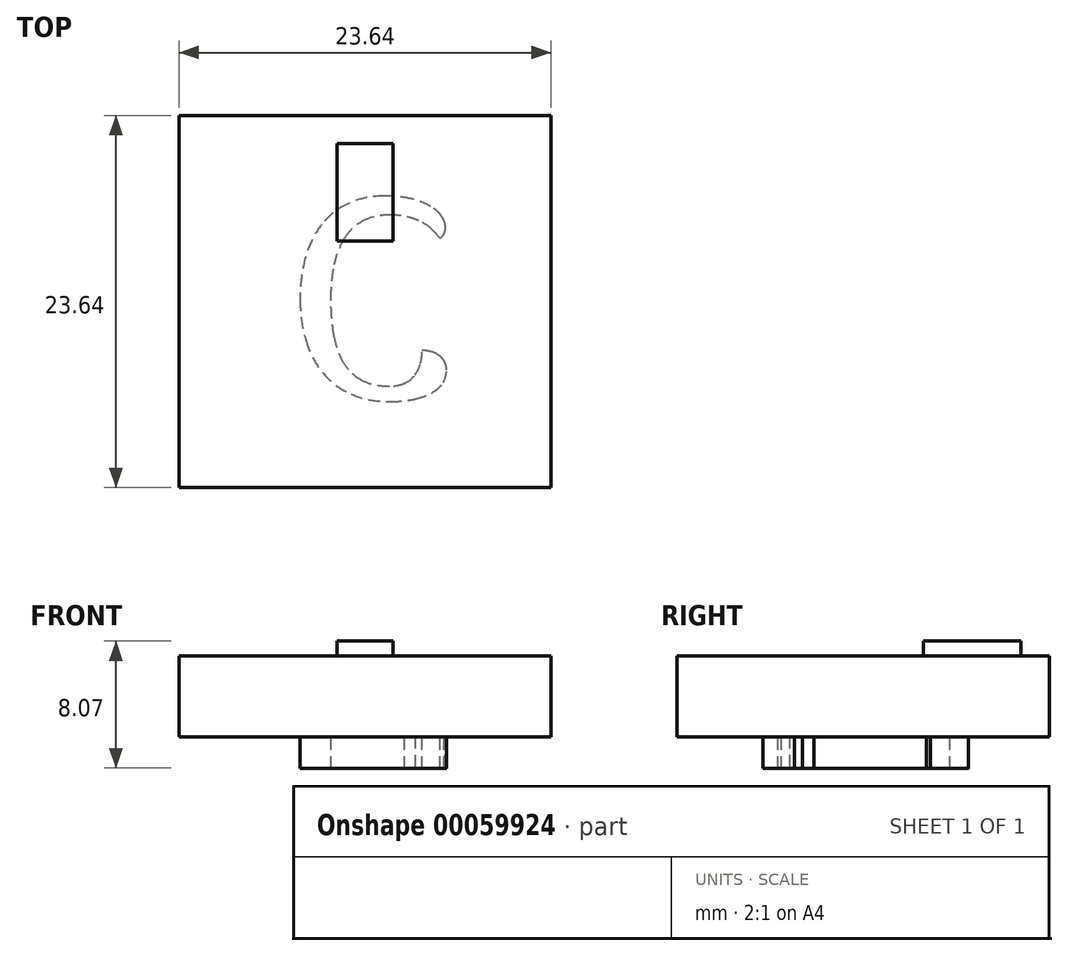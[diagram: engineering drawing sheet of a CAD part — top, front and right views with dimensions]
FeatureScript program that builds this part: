
annotation { "Feature Type Name" : "Feature", "Feature Type Description" : "" }
export const myFeature = defineFeature(function(context is Context, id is Id, definition is map)
    precondition{}
    {
        {
            var Q0;
            Q0=qCreatedBy(makeId("Top.planeOp"),FACE);
            var sketch = newSketch(context, id + "F0", { "sketchPlane" : qUnion([Q0])});
            skCircle(sketch, "E0.cCircle", {"center": v(0, 0) * mm, "radius": 11.82 * mm, "construction": true});
            skLineSegment(sketch, "E0.0", {"start": v(-11.82, 11.82) * mm, "end": v(11.82, 11.82) * mm});
            skLineSegment(sketch, "E0.1", {"start": v(11.82, 11.82) * mm, "end": v(11.82, -11.82) * mm});
            skLineSegment(sketch, "E0.2", {"start": v(11.82, -11.82) * mm, "end": v(-11.82, -11.82) * mm});
            skLineSegment(sketch, "E0.3", {"start": v(-11.82, -11.82) * mm, "end": v(-11.82, 11.82) * mm});
            skPoint(sketch, "E0.0.midPoint", {"position": v(0, 11.82) * mm});
            skSolve(sketch);
        }
        {
            var Q0;
            Q0 = qSketchRegion(id + "F0", true);
            var Q1;
            Q1 = qConstructionFilter(qBodyType(qCreatedBy(id + "F0" ,EDGE), BodyType.WIRE), ConstructionObject.NO);
            extrude(context, id + "F1", {"entities" : qUnion([Q0]), "surfaceEntities" : qUnion([Q1]), "endBound" : BoundingType.SYMMETRIC, "depth" : 5.14 * mm});
        }
        {
            var Q0;
            Q0=qCreatedBy(makeId("Top.planeOp"),FACE);
            var sketch = newSketch(context, id + "F2", { "sketchPlane" : qUnion([Q0])});
            skLineSegment(sketch, "E1", {"start": v(-1.78, 10.03) * mm, "end": v(-1.78, 3.83) * mm});
            skLineSegment(sketch, "E2", {"start": v(-1.78, 3.83) * mm, "end": v(0, 3.83) * mm});
            skLineSegment(sketch, "E3", {"start": v(-1.78, 10.03) * mm, "end": v(0, 10.03) * mm});
            skLineSegment(sketch, "E4.MirrorCS", {"start": v(1.78, 10.03) * mm, "end": v(1.78, 3.83) * mm});
            skLineSegment(sketch, "E5.MirrorCS", {"start": v(1.78, 10.03) * mm, "end": v(0, 10.03) * mm});
            skLineSegment(sketch, "E6.MirrorCS", {"start": v(1.78, 3.83) * mm, "end": v(0, 3.83) * mm});
            skSolve(sketch);
        }
        {
            var Q0;
            Q0 = qSketchRegion(id + "F2", true);
            extrude(context, id + "F3", {"entities" : qUnion([Q0]), "operationType" : NewBodyOperationType.ADD, "depth" : 3.5 * mm});
        }
        {
            var Q0;
            Q0=makeQuery(id+"F1.opExtrude","CAP_FACE",FACE,{"disambiguationData":[OSD([sQuery(id+"F0.wireOp",EDGE,"E0.0"),sQuery(id+"F0.wireOp",EDGE,"E0.1"),sQuery(id+"F0.wireOp",EDGE,"E0.2"),sQuery(id+"F0.wireOp",EDGE,"E0.3")])],"isStart":true});
            var sketch = newSketch(context, id + "F4", { "sketchPlane" : qUnion([Q0])});
            skText(sketch, "E7", { "text": "C", "fontName": "NotoSerif-Regular.ttf"});
            const initialGuessF4  = {"E7": [-0.00514, -0.00652, 1, 0, 0.0128]};
            skSetInitialGuess(sketch, initialGuessF4);
            skSolve(sketch);
        }
        {
            var Q0;
            Q0 = qSketchRegion(id + "F4", true);
            extrude(context, id + "F5", {"entities" : qUnion([Q0]), "operationType" : NewBodyOperationType.ADD, "depth" : 2 * mm});
        }
    });
